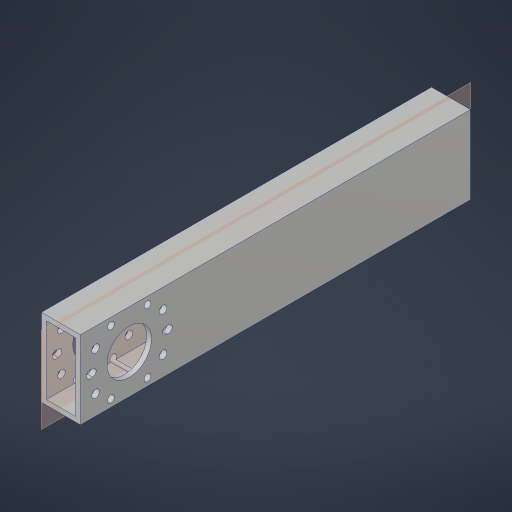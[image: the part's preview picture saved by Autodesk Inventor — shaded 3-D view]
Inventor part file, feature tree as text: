
AUTODESK INVENTOR PART (.ipt)
format: ipt  version: 2023.4 (Build 274418000, 418)  size: 231,936 bytes
history: native  units: in
note: dims shown in document units (in); Inventor stores cm internally (conversion verified against a paired STEP export)
features: hole x3, extrude x1, sketch x1, projected_geometry x1
ambient origin geometry x8: Origin, YZ Plane, XZ Plane, XY Plane, X Axis, Y Axis, Z Axis, Center Point
bodies: Solid1 (feature_tree)
feature tree (6):
  extrude  "Extrusion1"  Depth=1.0in
  sketch  "Sketch2"  dims[d4=0.0in d5=1.25in d6=1.14in d7=0.75in d8=0.375in d9=0.25in d10=0.5635in d11=1.0in d12=0.8108in d13=1.875in d14=2.0in d15=4.7244in d17=360.0deg d19=2.3622in d21=360.0deg d23=0.201in d24=0.75in d25=0.332in d26=0.25in d27=0.5635in d28=1.0in d29=0.8108in d30=0.177in d31=0.75in d32=0.385in d33=0.25in d34=0.5635in d35=1.0in d36=0.8108in]
  hole  "Hole1"  [1 undecoded]
  hole  "Hole2"  [1 undecoded]
  hole  "Hole3"  [1 undecoded]
  projected_geometry  "Project Cut Edges1"
note: 3 required parameter values undecoded (feature->parameter linkage not recoverable at this tier; creation-order binding heuristic only, values carry confidence <= 0.55)
